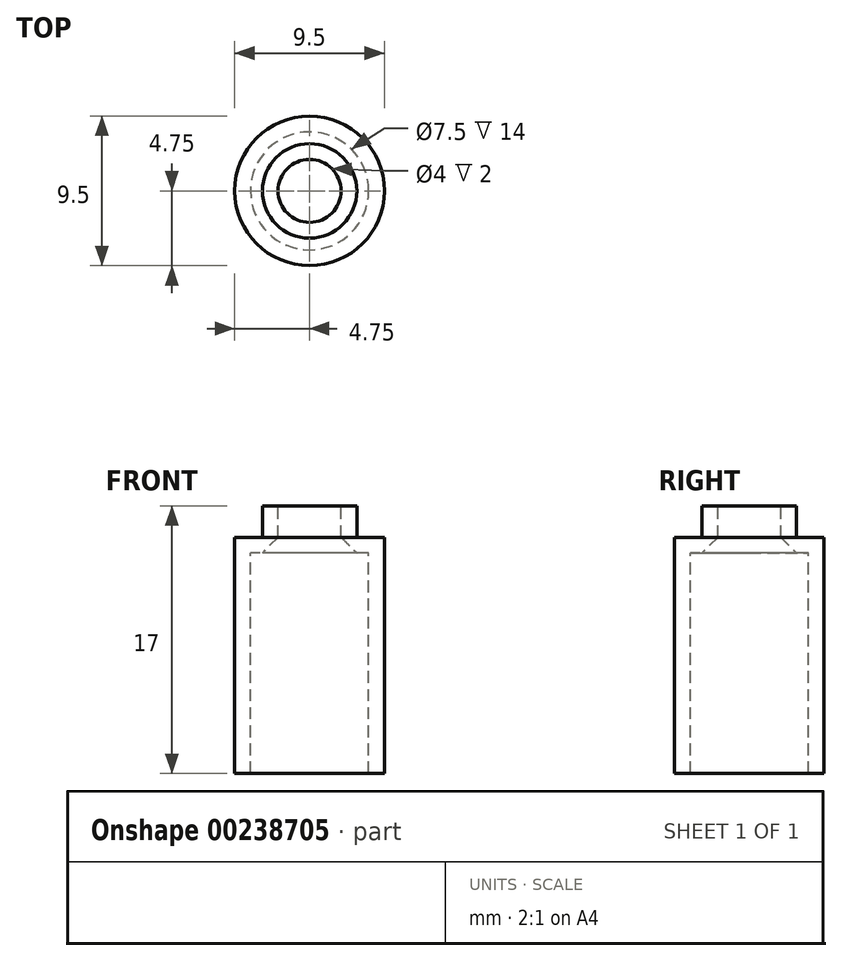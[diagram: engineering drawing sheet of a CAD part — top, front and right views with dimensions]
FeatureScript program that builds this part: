
annotation { "Feature Type Name" : "Feature", "Feature Type Description" : "" }
export const myFeature = defineFeature(function(context is Context, id is Id, definition is map)
    precondition{}
    {
        {
            var Q0;
            Q0=qCreatedBy(makeId("Top.planeOp"),FACE);
            var sketch = newSketch(context, id + "F0", { "sketchPlane" : qUnion([Q0])});
            skCircle(sketch, "E0", {"center": v(0, 0) * mm, "radius": 4.75 * mm});
            skCircle(sketch, "E1", {"center": v(0, 0) * mm, "radius": 3.75 * mm});
            skCircle(sketch, "E2", {"center": v(0, 0) * mm, "radius": 2 * mm});
            skCircle(sketch, "E3", {"center": v(0, 0) * mm, "radius": 3 * mm});
            skSolve(sketch);
        }
        {
            var Q0;
            Q0=qSketchRegion(id+"F0",true);
            extrude(context, id + "F1", {"entities" : qUnion([Q0]), "oppositeDirection" : true, "depth" : 15 * mm});
        }
        {
            var Q0;
            Q0=makeQuery(id+"F0.imprint","IMPRINT",FACE,{"disambiguationData":[TD([[makeQuery(id+"F0.imprint","IMPRINT",EDGE,{"derivedFrom":sQuery(id+"F0.wireOp",EDGE,"E1")}),1.0]])]});
            var Q1;
            Q1=makeQuery(id+"F0.imprint","IMPRINT",FACE,{"disambiguationData":[TD([[makeQuery(id+"F0.imprint","IMPRINT",EDGE,{"derivedFrom":sQuery(id+"F0.wireOp",EDGE,"E2")}),-1.0]])]});
            extrude(context, id + "F2", {"entities" : qUnion([Q0, Q1]), "operationType" : NewBodyOperationType.ADD, "oppositeDirection" : true, "depth" : 1 * mm});
        }
        {
            var Q0;
            Q0=makeQuery(id+"F0.imprint","IMPRINT",FACE,{"disambiguationData":[TD([[makeQuery(id+"F0.imprint","IMPRINT",EDGE,{"derivedFrom":sQuery(id+"F0.wireOp",EDGE,"E2")}),-1.0]])]});
            extrude(context, id + "F3", {"entities" : qUnion([Q0]), "operationType" : NewBodyOperationType.ADD, "depth" : 2 * mm});
        }
        {
            var Q0;
            Q0=makeQuery(id+"F2.opExtrude","CAP_EDGE",EDGE,{"disambiguationData":[OSD([sQuery(id+"F0.wireOp",EDGE,"E2")])],"isStart":false});
            chamfer(context, id + "F4", {"entities" : qUnion([Q0]), "chamferType" : ChamferType.TWO_OFFSETS, "width1" : 1 * mm, "oppositeDirection" : false, "width2" : 1 * mm, "tangentPropagation" : true});
        }
    });
